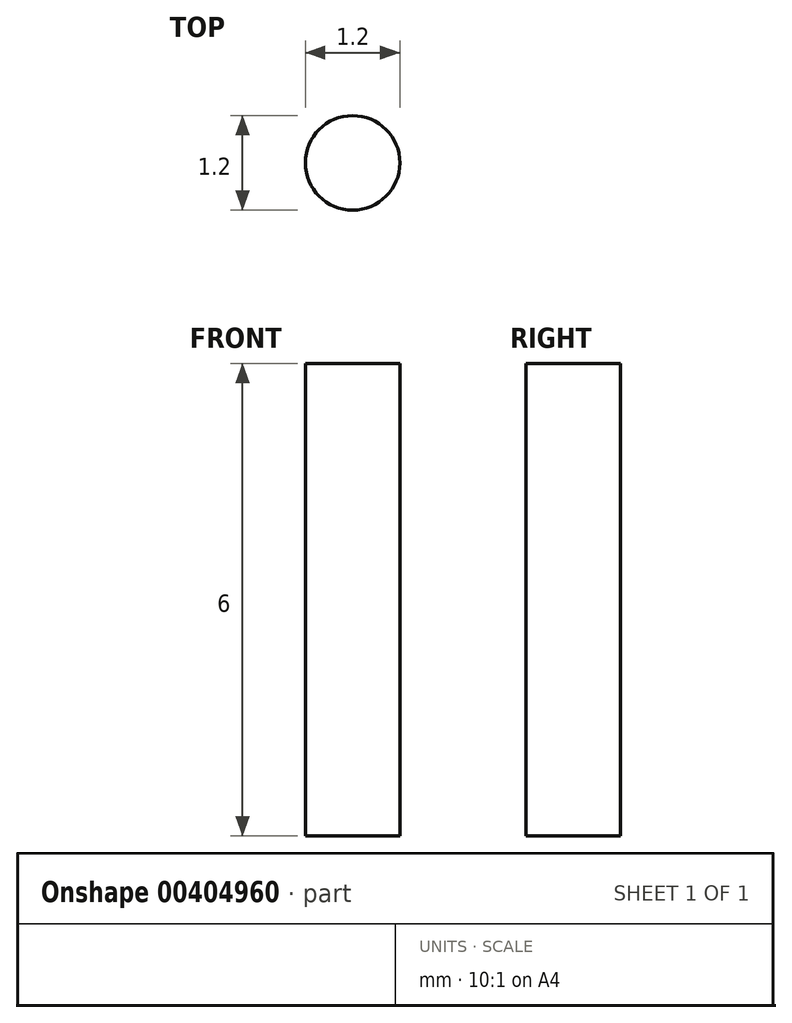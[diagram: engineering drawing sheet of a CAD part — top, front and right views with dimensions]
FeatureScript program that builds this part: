
annotation { "Feature Type Name" : "Feature", "Feature Type Description" : "" }
export const myFeature = defineFeature(function(context is Context, id is Id, definition is map)
    precondition{}
    {
        {
            var Q0;
            Q0=qCreatedBy(makeId("Top.planeOp"),FACE);
            var sketch = newSketch(context, id + "F0", { "sketchPlane" : qUnion([Q0])});
            skCircle(sketch, "E0", {"center": v(0, 0) * mm, "radius": 0.6 * mm});
            skSolve(sketch);
        }
        {
            var Q0;
            Q0=qSketchRegion(id+"F0",true);
            extrude(context, id + "F1", {"entities" : qUnion([Q0]), "depth" : 6 * mm});
        }
    });
